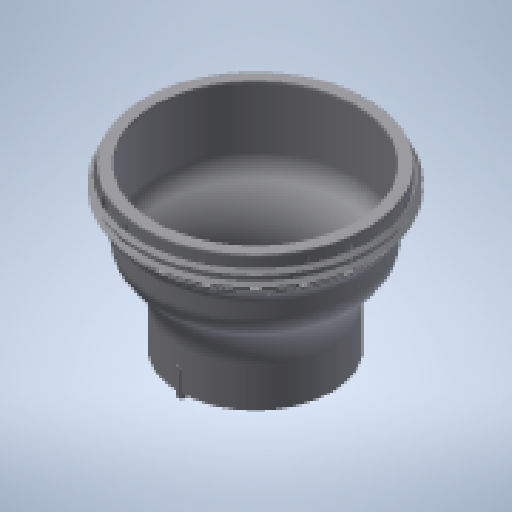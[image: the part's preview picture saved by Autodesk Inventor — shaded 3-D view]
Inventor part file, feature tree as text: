
AUTODESK INVENTOR PART (.ipt)
format: ipt  version: 2023.3 (Build 273359000, 359)  size: 1,307,648 bytes
history: native  units: mm
features: other x9, boolean_combine x2, revolve x1, sketch x1
ambient origin geometry x8: Origin, YZ Plane, XZ Plane, XY Plane, X Axis, Y Axis, Z Axis, Center Point
bodies: Solid4 (feature_tree), Solid1 (feature_tree), Solid3 (feature_tree)
feature tree (13):
  other  "Sealing_ring_20x1_silicone_i.ipt"
  other  "Mold_1_Sealing_ring_20x1_silicone_x.ipt"
  other  "Mold_2_Sealing_ring_20x1_silicone_h.ipt"
  boolean_combine  "Combine1"
  revolve  "Revolution1"  [1 undecoded]
  boolean_combine  "Combine2"
  other  "Solid1::Sealing_ring_20x1_silicone_i.ipt"
  other  "TaggingFeature1"
  other  "Solid1::Mold_1_Sealing_ring_20x1_silicone_x.ipt"
  other  "TaggingFeature2"
  other  "Solid3::Mold_2_Sealing_ring_20x1_silicone_h.ipt"
  other  "TaggingFeature3"
  sketch  "Sketch1"  dims[d0=10.0mm d1=10.0mm d2=10.0mm d3=360.0deg d4=0.872665mm d5=0.872665mm]
note: 1 required parameter value undecoded (feature->parameter linkage not recoverable at this tier; creation-order binding heuristic only, values carry confidence <= 0.55)
